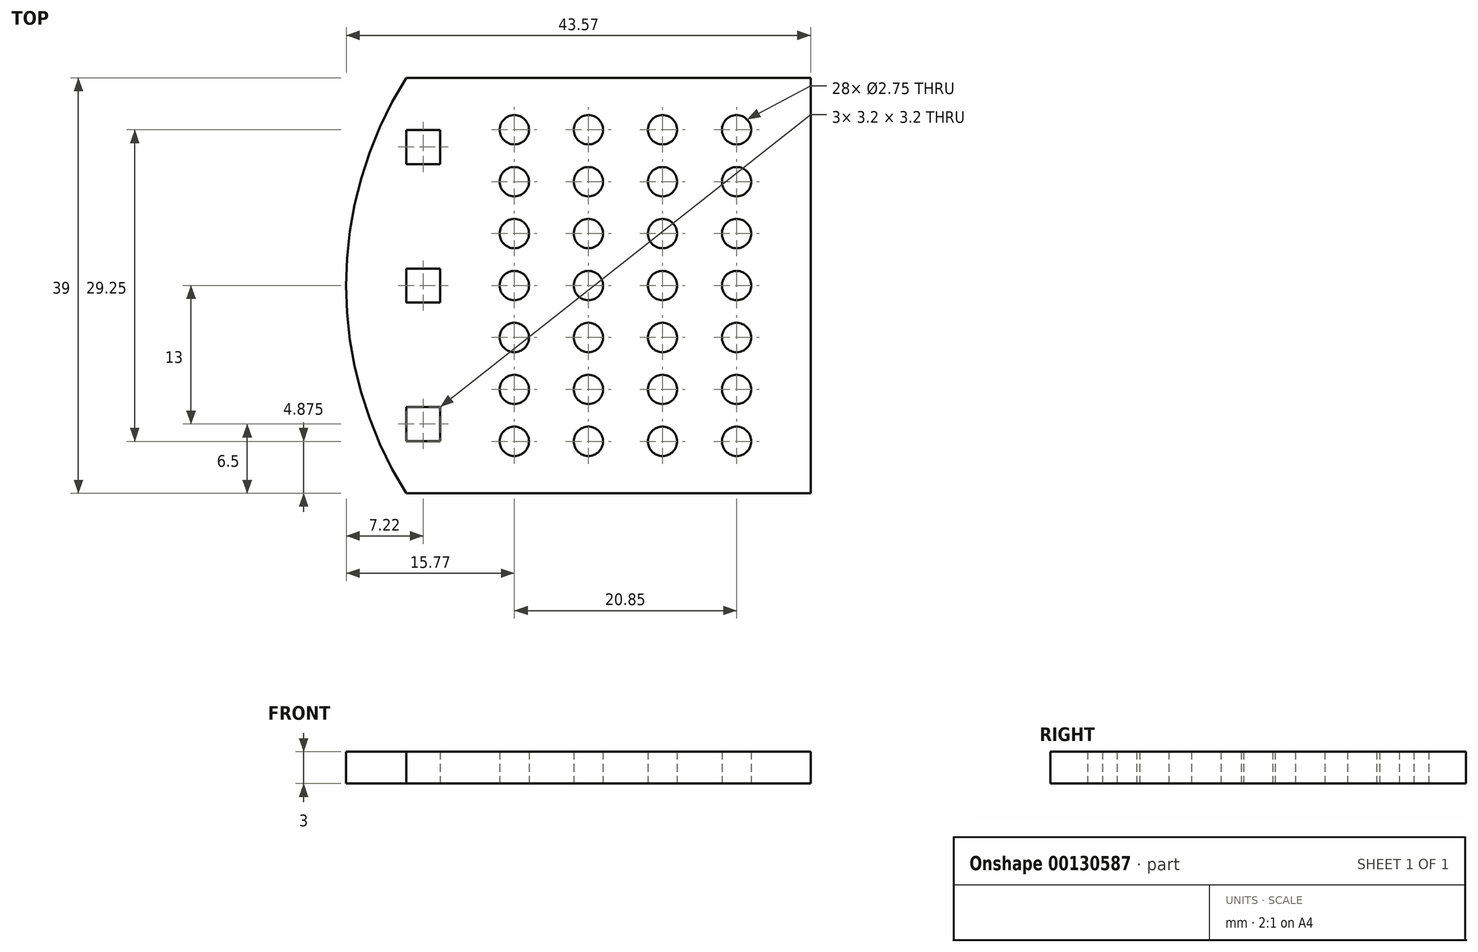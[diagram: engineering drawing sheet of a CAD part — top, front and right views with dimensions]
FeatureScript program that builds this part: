
annotation { "Feature Type Name" : "Feature", "Feature Type Description" : "" }
export const myFeature = defineFeature(function(context is Context, id is Id, definition is map)
    precondition{}
    {
        {
            var Q0;
            Q0=qCreatedBy(makeId("Top.planeOp"),FACE);
            var sketch = newSketch(context, id + "F0", { "sketchPlane" : qUnion([Q0])});
            skLineSegment(sketch, "E0", {"start": v(-27.8, -19.5) * mm, "end": v(-31, -19.5) * mm});
            skLineSegment(sketch, "E1", {"start": v(-27.8, 19.5) * mm, "end": v(-31, 19.5) * mm});
            skLineSegment(sketch, "E2", {"start": v(-27.8, 19.5) * mm, "end": v(-13.9, 19.5) * mm, "construction": true});
            skLineSegment(sketch, "E3", {"start": v(-13.9, 19.5) * mm, "end": v(0, 19.5) * mm, "construction": true});
            skLineSegment(sketch, "E4", {"start": v(0, 19.5) * mm, "end": v(0, -17) * mm, "construction": true});
            skLineSegment(sketch, "E5", {"start": v(-13.9, 19.5) * mm, "end": v(-13.9, -17.78) * mm, "construction": true});
            skLineSegment(sketch, "E6", {"start": v(-6.95, 19.5) * mm, "end": v(-6.95, -17.21) * mm, "construction": true});
            skLineSegment(sketch, "E7", {"start": v(-20.85, 19.5) * mm, "end": v(-20.85, -18.58) * mm, "construction": true});
            skCircle(sketch, "E8", {"center": v(-20.85, -14.62) * mm, "radius": 1.38 * mm});
            skCircle(sketch, "E9", {"center": v(-13.9, -14.62) * mm, "radius": 1.38 * mm});
            skCircle(sketch, "E10", {"center": v(-6.95, -14.62) * mm, "radius": 1.38 * mm});
            skCircle(sketch, "E11", {"center": v(-20.85, -9.75) * mm, "radius": 1.38 * mm});
            skCircle(sketch, "E12", {"center": v(-13.9, -9.75) * mm, "radius": 1.38 * mm});
            skCircle(sketch, "E13", {"center": v(-6.95, -9.75) * mm, "radius": 1.38 * mm});
            skCircle(sketch, "E14", {"center": v(-20.85, -4.88) * mm, "radius": 1.38 * mm});
            skCircle(sketch, "E15", {"center": v(-13.9, -4.88) * mm, "radius": 1.38 * mm});
            skCircle(sketch, "E16", {"center": v(-20.85, 0) * mm, "radius": 1.38 * mm});
            skCircle(sketch, "E17", {"center": v(-13.9, 0) * mm, "radius": 1.38 * mm});
            skCircle(sketch, "E18.MirrorC", {"center": v(-13.9, 14.63) * mm, "radius": 1.38 * mm});
            skCircle(sketch, "E19.MirrorC", {"center": v(-13.9, 9.75) * mm, "radius": 1.38 * mm});
            skCircle(sketch, "E20.MirrorC", {"center": v(-20.85, 9.75) * mm, "radius": 1.38 * mm});
            skCircle(sketch, "E21.MirrorC", {"center": v(-6.95, 9.75) * mm, "radius": 1.38 * mm});
            skCircle(sketch, "E22.MirrorC", {"center": v(-6.95, 14.63) * mm, "radius": 1.38 * mm});
            skCircle(sketch, "E23.MirrorC", {"center": v(-20.85, 14.63) * mm, "radius": 1.38 * mm});
            skCircle(sketch, "E24.MirrorC", {"center": v(-20.85, 4.88) * mm, "radius": 1.38 * mm});
            skLineSegment(sketch, "E25.MirrorCS", {"start": v(-13.9, -19.5) * mm, "end": v(-13.9, 17.78) * mm, "construction": true});
            skLineSegment(sketch, "E26.MirrorCS", {"start": v(-20.85, -19.5) * mm, "end": v(-20.85, 18.58) * mm, "construction": true});
            skCircle(sketch, "E27.MirrorC", {"center": v(-13.9, 4.88) * mm, "radius": 1.38 * mm});
            skLineSegment(sketch, "E28", {"start": v(-27.8, 0) * mm, "end": v(-39.8, 0) * mm, "construction": true});
            skLineSegment(sketch, "E29", {"start": v(-27.8, 4.88) * mm, "end": v(5.02, 4.88) * mm, "construction": true});
            skLineSegment(sketch, "E30", {"start": v(-27.8, 0) * mm, "end": v(6.97, 0) * mm, "construction": true});
            skLineSegment(sketch, "E31", {"start": v(-27.8, -4.88) * mm, "end": v(6.16, -4.87) * mm, "construction": true});
            skLineSegment(sketch, "E32", {"start": v(-27.8, -9.75) * mm, "end": v(7.45, -9.75) * mm, "construction": true});
            skCircle(sketch, "E33", {"center": v(-6.95, 4.88) * mm, "radius": 1.38 * mm});
            skCircle(sketch, "E34", {"center": v(-6.95, 0) * mm, "radius": 1.38 * mm});
            skCircle(sketch, "E35", {"center": v(-6.95, -4.88) * mm, "radius": 1.38 * mm});
            skLineSegment(sketch, "E36", {"start": v(0, -19.5) * mm, "end": v(-27.8, -19.5) * mm});
            skLineSegment(sketch, "E37", {"start": v(0, 19.5) * mm, "end": v(-31, 19.5) * mm});
            skLineSegment(sketch, "E38", {"start": v(-27.8, -19.5) * mm, "end": v(-27.8, 19.5) * mm, "construction": true});
            skLineSegment(sketch, "E39", {"start": v(-27.8, 0) * mm, "end": v(-27.8, 13) * mm, "construction": true});
            skLineSegment(sketch, "E40", {"start": v(-27.8, 13) * mm, "end": v(-29.4, 13) * mm, "construction": true});
            skLineSegment(sketch, "E41", {"start": v(-27.8, 0) * mm, "end": v(-27.8, -13) * mm, "construction": true});
            skLineSegment(sketch, "E42", {"start": v(-27.8, -13) * mm, "end": v(-29.4, -13) * mm, "construction": true});
            skLineSegment(sketch, "E43", {"start": v(-29.4, -13) * mm, "end": v(-29.4, -11.4) * mm, "construction": true});
            skLineSegment(sketch, "E44", {"start": v(-29.4, -11.4) * mm, "end": v(-27.8, -11.4) * mm});
            skLineSegment(sketch, "E45", {"start": v(-27.8, -11.4) * mm, "end": v(-27.8, -14.6) * mm});
            skLineSegment(sketch, "E46", {"start": v(-27.8, -14.6) * mm, "end": v(-31, -14.6) * mm});
            skLineSegment(sketch, "E47", {"start": v(-31, -14.6) * mm, "end": v(-31, -11.4) * mm});
            skLineSegment(sketch, "E48", {"start": v(-31, -11.4) * mm, "end": v(-29.4, -11.4) * mm});
            skLineSegment(sketch, "E49.MirrorCS", {"start": v(-29.4, 13) * mm, "end": v(-29.4, 11.4) * mm, "construction": true});
            skLineSegment(sketch, "E50.MirrorCS", {"start": v(-27.8, 11.4) * mm, "end": v(-27.8, 14.6) * mm});
            skLineSegment(sketch, "E51.MirrorCS", {"start": v(-29.4, 11.4) * mm, "end": v(-27.8, 11.4) * mm});
            skLineSegment(sketch, "E52.MirrorCS", {"start": v(-31, 14.6) * mm, "end": v(-31, 11.4) * mm});
            skLineSegment(sketch, "E53.MirrorCS", {"start": v(-31, 11.4) * mm, "end": v(-29.4, 11.4) * mm});
            skLineSegment(sketch, "E54.MirrorCS", {"start": v(-27.8, 14.6) * mm, "end": v(-31, 14.6) * mm});
            skArc(sketch, "E55", {"start": v(-31, -19.5) * mm, "mid": v(-36.62, 0) * mm, "end": v(-31, 19.5) * mm});
            skLineSegment(sketch, "E56", {"start": v(0, 19.5) * mm, "end": v(6.95, 19.5) * mm, "construction": true});
            skLineSegment(sketch, "E57", {"start": v(6.95, 19.5) * mm, "end": v(6.95, -19.5) * mm, "construction": true});
            skLineSegment(sketch, "E58", {"start": v(6.95, -19.5) * mm, "end": v(0, -19.5) * mm, "construction": true});
            skLineSegment(sketch, "E59", {"start": v(-20.85, 14.63) * mm, "end": v(0, 14.63) * mm, "construction": true});
            skLineSegment(sketch, "E60", {"start": v(-20.85, 9.75) * mm, "end": v(0, 9.75) * mm, "construction": true});
            skLineSegment(sketch, "E61", {"start": v(-20.85, -14.62) * mm, "end": v(0, -14.62) * mm, "construction": true});
            skCircle(sketch, "E62", {"center": v(0, 14.63) * mm, "radius": 1.38 * mm});
            skCircle(sketch, "E63", {"center": v(0, 9.75) * mm, "radius": 1.38 * mm});
            skCircle(sketch, "E64", {"center": v(0, 4.88) * mm, "radius": 1.38 * mm});
            skCircle(sketch, "E65", {"center": v(0, 0) * mm, "radius": 1.38 * mm});
            skCircle(sketch, "E66", {"center": v(0, -4.87) * mm, "radius": 1.38 * mm});
            skCircle(sketch, "E67", {"center": v(0, -9.75) * mm, "radius": 1.38 * mm});
            skCircle(sketch, "E68", {"center": v(0, -14.62) * mm, "radius": 1.38 * mm});
            skLineSegment(sketch, "E69", {"start": v(6.95, 19.5) * mm, "end": v(6.95, -19.5) * mm});
            skLineSegment(sketch, "E70", {"start": v(0, -19.5) * mm, "end": v(6.95, -19.5) * mm});
            skLineSegment(sketch, "E71", {"start": v(0, 19.5) * mm, "end": v(6.95, 19.5) * mm});
            skLineSegment(sketch, "E72", {"start": v(-29.4, 13) * mm, "end": v(-29.4, -13) * mm, "construction": true});
            skLineSegment(sketch, "E73", {"start": v(-29.4, 0) * mm, "end": v(-29.4, 1.6) * mm, "construction": true});
            skLineSegment(sketch, "E74", {"start": v(-29.4, 1.6) * mm, "end": v(-27.8, 1.6) * mm, "construction": true});
            skLineSegment(sketch, "E75", {"start": v(-29.4, 1.6) * mm, "end": v(-27.8, 1.6) * mm});
            skLineSegment(sketch, "E76", {"start": v(-27.8, 1.6) * mm, "end": v(-27.8, -1.6) * mm});
            skLineSegment(sketch, "E77", {"start": v(-27.8, -1.6) * mm, "end": v(-31, -1.6) * mm});
            skLineSegment(sketch, "E78", {"start": v(-31, -1.6) * mm, "end": v(-31, 1.6) * mm});
            skLineSegment(sketch, "E79", {"start": v(-31, 1.6) * mm, "end": v(-29.4, 1.6) * mm});
            skSolve(sketch);
        }
        {
            var Q0;
            Q0=qSketchRegion(id+"F0",true);
            extrude(context, id + "F1", {"entities" : qUnion([Q0]), "endBound" : BoundingType.SYMMETRIC, "depth" : 3 * mm});
        }
    });
